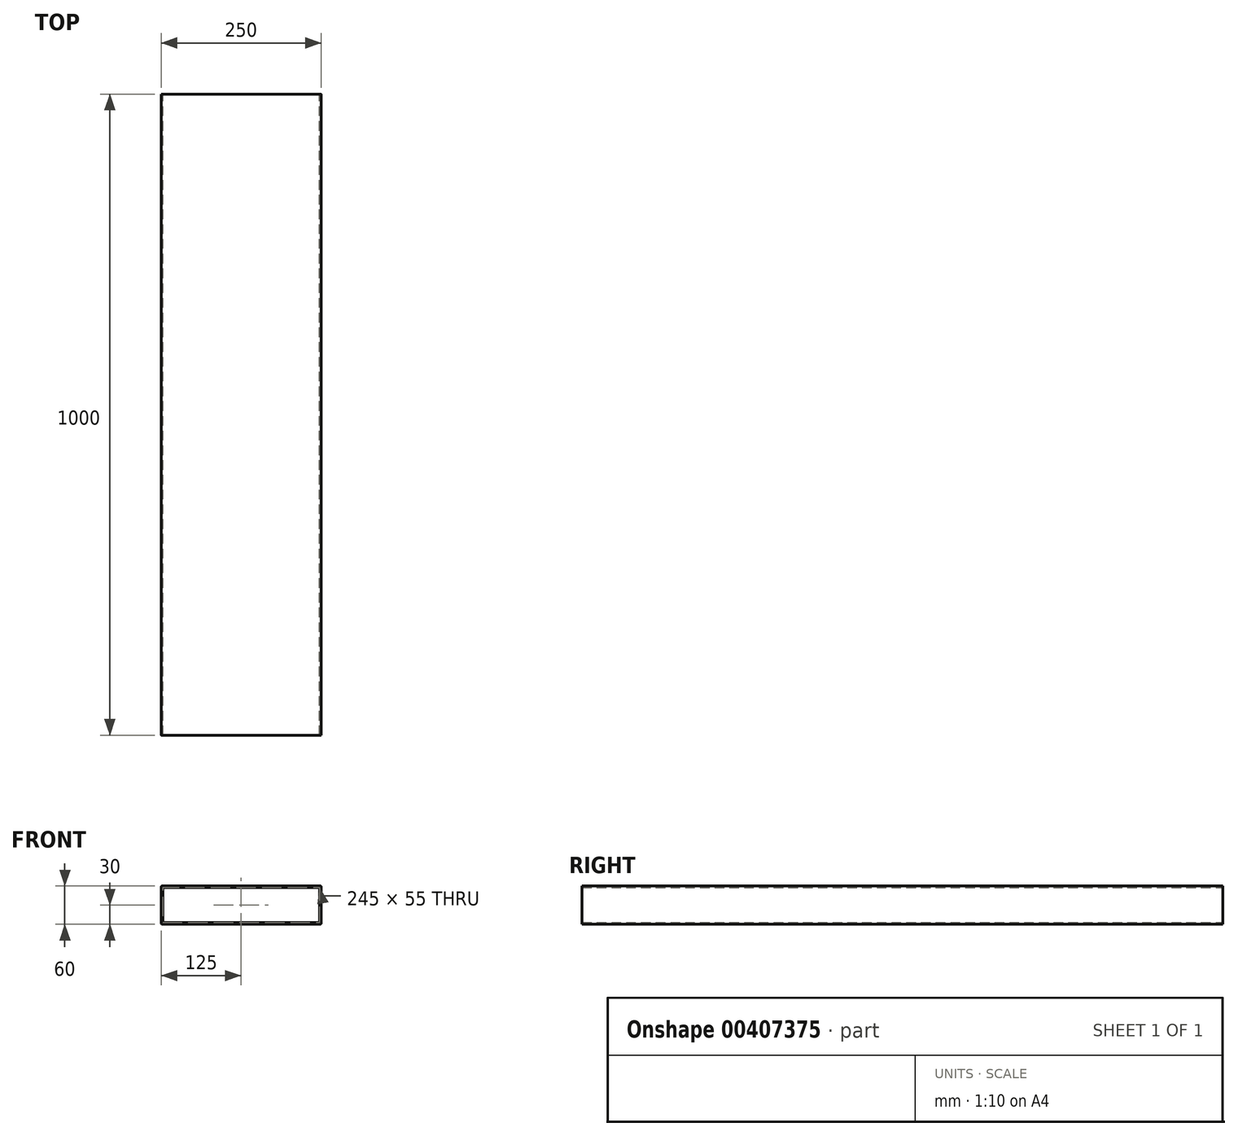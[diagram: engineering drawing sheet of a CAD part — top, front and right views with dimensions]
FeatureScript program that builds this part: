
annotation { "Feature Type Name" : "Feature", "Feature Type Description" : "" }
export const myFeature = defineFeature(function(context is Context, id is Id, definition is map)
    precondition{}
    {
        {
            var Q0;
            Q0=qCreatedBy(makeId("Front.planeOp"),FACE);
            var sketch = newSketch(context, id + "F0", { "sketchPlane" : qUnion([Q0])});
            skLineSegment(sketch, "E0.bottom", {"start": v(250, 60) * mm, "end": v(0, 60) * mm});
            skLineSegment(sketch, "E0.top", {"start": v(250, 0) * mm, "end": v(0, 0) * mm});
            skLineSegment(sketch, "E0.left", {"start": v(250, 60) * mm, "end": v(250, 0) * mm});
            skLineSegment(sketch, "E0.right", {"start": v(0, 60) * mm, "end": v(0, 0) * mm});
            skSolve(sketch);
        }
        {
            var Q0;
            Q0=makeQuery(id+"F0.imprint","IMPRINT",FACE,{"disambiguationData":[TD([[makeQuery(id+"F0.imprint","IMPRINT",EDGE,{"derivedFrom":sQuery(id+"F0.wireOp",EDGE,"E0.bottom")}),1.0]])]});
            extrude(context, id + "F1", {"entities" : qUnion([Q0]), "depth" : 1000 * mm});
        }
        {
            var Q0;
            Q0=makeQuery(id+"F1.opExtrude","CAP_FACE",FACE,{"disambiguationData":[OSD([sQuery(id+"F0.wireOp",EDGE,"E0.bottom"),sQuery(id+"F0.wireOp",EDGE,"E0.top"),sQuery(id+"F0.wireOp",EDGE,"E0.left"),sQuery(id+"F0.wireOp",EDGE,"E0.right")])],"isStart":false});
            var Q1;
            Q1=makeQuery(id+"F1.opExtrude","CAP_FACE",FACE,{"disambiguationData":[OSD([sQuery(id+"F0.wireOp",EDGE,"E0.bottom"),sQuery(id+"F0.wireOp",EDGE,"E0.top"),sQuery(id+"F0.wireOp",EDGE,"E0.left"),sQuery(id+"F0.wireOp",EDGE,"E0.right")])],"isStart":true});
            shell(context, id + "F2", {"entities" : qUnion([Q0, Q1]), "thickness" : 2.5 * mm});
        }
        {
            var Q0;
            Q0=makeQuery(id+"F1.opExtrude","SWEPT_EDGE",EDGE,{"disambiguationData":[OSD([sQuery(id+"F0.wireOp",EDGE,"E0.bottom"),sQuery(id+"F0.wireOp",EDGE,"E0.right")])]});
            var Q1;
            Q1=makeQuery(id+"F1.opExtrude","SWEPT_EDGE",EDGE,{"disambiguationData":[OSD([sQuery(id+"F0.wireOp",EDGE,"E0.bottom"),sQuery(id+"F0.wireOp",EDGE,"E0.left")])]});
            var Q2;
            Q2=makeQuery(id+"F1.opExtrude","SWEPT_EDGE",EDGE,{"disambiguationData":[OSD([sQuery(id+"F0.wireOp",EDGE,"E0.top"),sQuery(id+"F0.wireOp",EDGE,"E0.left")])]});
            var Q3;
            Q3=makeQuery(id+"F1.opExtrude","SWEPT_EDGE",EDGE,{"disambiguationData":[OSD([sQuery(id+"F0.wireOp",EDGE,"E0.top"),sQuery(id+"F0.wireOp",EDGE,"E0.right")])]});
            fillet(context, id + "F3", {"entities" : qUnion([Q0, Q1, Q2, Q3]), "radius" : 2 * mm, "tangentPropagation" : true, "allowEdgeOverflow" : false});
        }
    });
